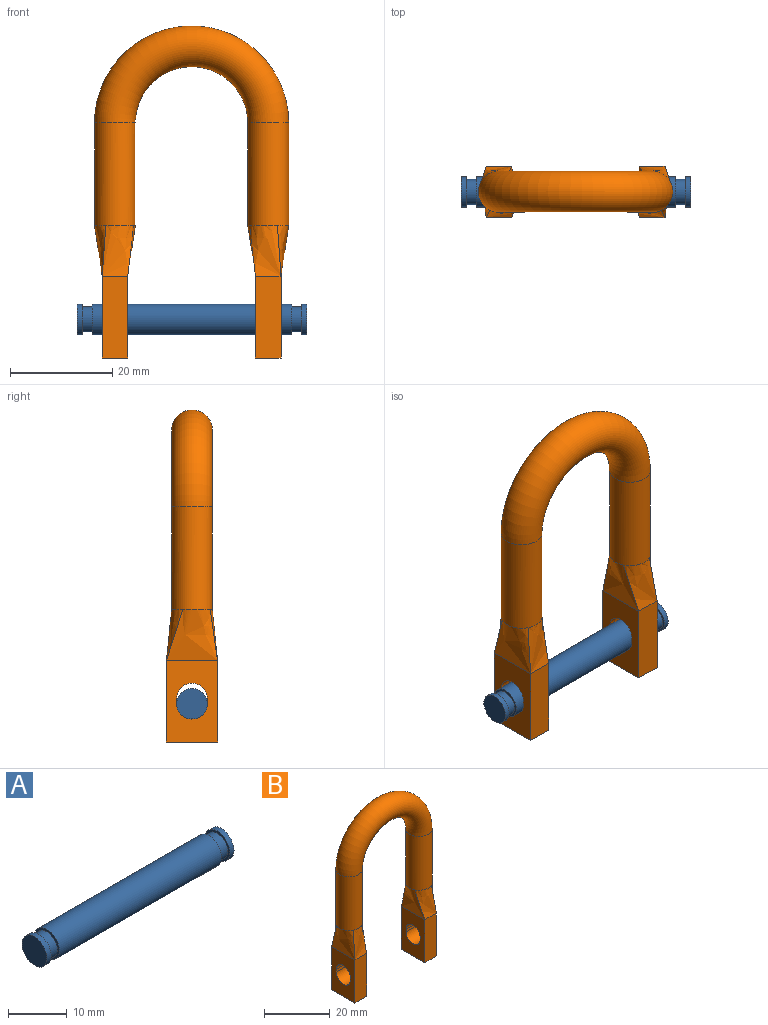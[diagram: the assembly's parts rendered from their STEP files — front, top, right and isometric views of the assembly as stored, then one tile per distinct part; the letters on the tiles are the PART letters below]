
ASSEMBLY  parts=2 mates=1
PART A: 11 faces, bbox 45x6x6 mm
  f0: plane 6x6mm, normal (-1,0,0), area 8.6mm2, adj f1,f10
  f1: cylinder r=2.5mm len=5mm, axis (-1,0,0), area 31.4mm2, adj f0,f2
  f2: plane 6x6mm, normal (1,0,0), area 8.6mm2, adj f1,f3
  f3: cylinder r=3mm len=39mm, axis (-1,0,0), area 735.1mm2, adj f2,f4
  f4: plane 6x6mm, normal (-1,0,0), area 8.6mm2, adj f3,f5
  f5: cylinder r=2.5mm len=5mm, axis (-1,0,0), area 31.4mm2, adj f4,f6
  f6: plane 6x6mm, normal (1,0,0), area 8.6mm2, adj f5,f7
  f7: cylinder r=3mm len=6mm, axis (-1,0,0), area 18.8mm2, adj f6,f8
  f8: plane 6x6mm, normal (-1,0,0), area 28.3mm2, adj f7
  f9: plane 6x6mm, normal (1,0,0), area 28.3mm2, adj f10
  f10: cylinder r=3mm len=6mm, axis (-1,0,0), area 18.8mm2, adj f0,f9
PART B: 29 faces, bbox 41.1x10x66.6 mm
  f0: plane 16x10mm, normal (1,0,0), area 125.7mm2, adj f1,f3,f4,f8,f25,f26,f27,f28
  f1: plane 16x5mm, normal (0,1,0), area 80mm2, adj f0,f2,f4,f5
  f2: plane 16x10mm, normal (-1,0,0), area 125.7mm2, adj f1,f3,f4,f6,f25,f26,f27,f28
  f3: plane 16x5mm, normal (0,-1,0), area 80mm2, adj f0,f2,f4,f7
  f4: plane 10x5mm, normal (0,0,-1), area 50mm2, adj f0,f1,f2,f3
  f5: bspline ~10x6.08mm, area 55.5mm2, adj f1,f6,f8,f10
  f6: bspline ~10x10mm, area 80mm2, adj f2,f5,f7,f10
  f7: bspline ~10x6.08mm, area 55.5mm2, adj f3,f6,f8,f10
  f8: bspline ~10x10mm, area 80mm2, adj f0,f5,f7,f10
  f9: cylinder r=4mm len=20mm, axis (0,0,1), area 502.7mm2, adj f11,f17,f18,f19,f20
  f10: cylinder r=4mm len=20mm, axis (0,0,1), area 502.7mm2, adj f5,f6,f7,f8,f11
  f11: torus R=15mm, axis (0,-1,0), area 1184.4mm2, adj f9,f10
  f12: plane 16x10mm, normal (-1,0,0), area 125.7mm2, adj f13,f15,f16,f20,f21,f22,f23,f24
  f13: plane 16x5mm, normal (0,1,0), area 80mm2, adj f12,f14,f16,f17
  f14: plane 16x10mm, normal (1,0,0), area 125.7mm2, adj f13,f15,f16,f18,f21,f22,f23,f24
  f15: plane 16x5mm, normal (0,-1,0), area 80mm2, adj f12,f14,f16,f19
  f16: plane 10x5mm, normal (0,0,-1), area 50mm2, adj f12,f13,f14,f15
  f17: bspline ~10x6.08mm, area 55.5mm2, adj f9,f13,f18,f20
  f18: bspline ~10x10mm, area 80mm2, adj f9,f14,f17,f19
  f19: bspline ~10x6.08mm, area 55.5mm2, adj f9,f15,f18,f20
  f20: bspline ~10x10mm, area 80mm2, adj f9,f12,f17,f19
  f21: plane 5x1mm, normal (0,-1,0), area 5mm2, adj f12,f14,f22,f24
  f22: cylinder r=3mm len=6mm, axis (1,0,0), area 47.1mm2, adj f12,f14,f21,f23
  f23: plane 5x1mm, normal (0,1,0), area 5mm2, adj f12,f14,f22,f24
  f24: cylinder r=3mm len=6mm, axis (1,0,0), area 47.1mm2, adj f12,f14,f21,f23
  f25: cylinder r=3mm len=6mm, axis (1,0,0), area 47.1mm2, adj f0,f2,f26,f28
  f26: plane 5x1mm, normal (0,1,0), area 5mm2, adj f0,f2,f25,f27
  f27: cylinder r=3mm len=6mm, axis (1,0,0), area 47.1mm2, adj f0,f2,f26,f28
  f28: plane 5x1mm, normal (0,-1,0), area 5mm2, adj f0,f2,f25,f27
PLACE A t=(-12.83,-5.5,-22.11)mm
PLACE B t=(-12.91,-5.5,6.39)mm
MATE cylindrical A.f1 <-> B.f22  axis (-1,0,0) through (-32.33,-5.5,-22.11)mm
